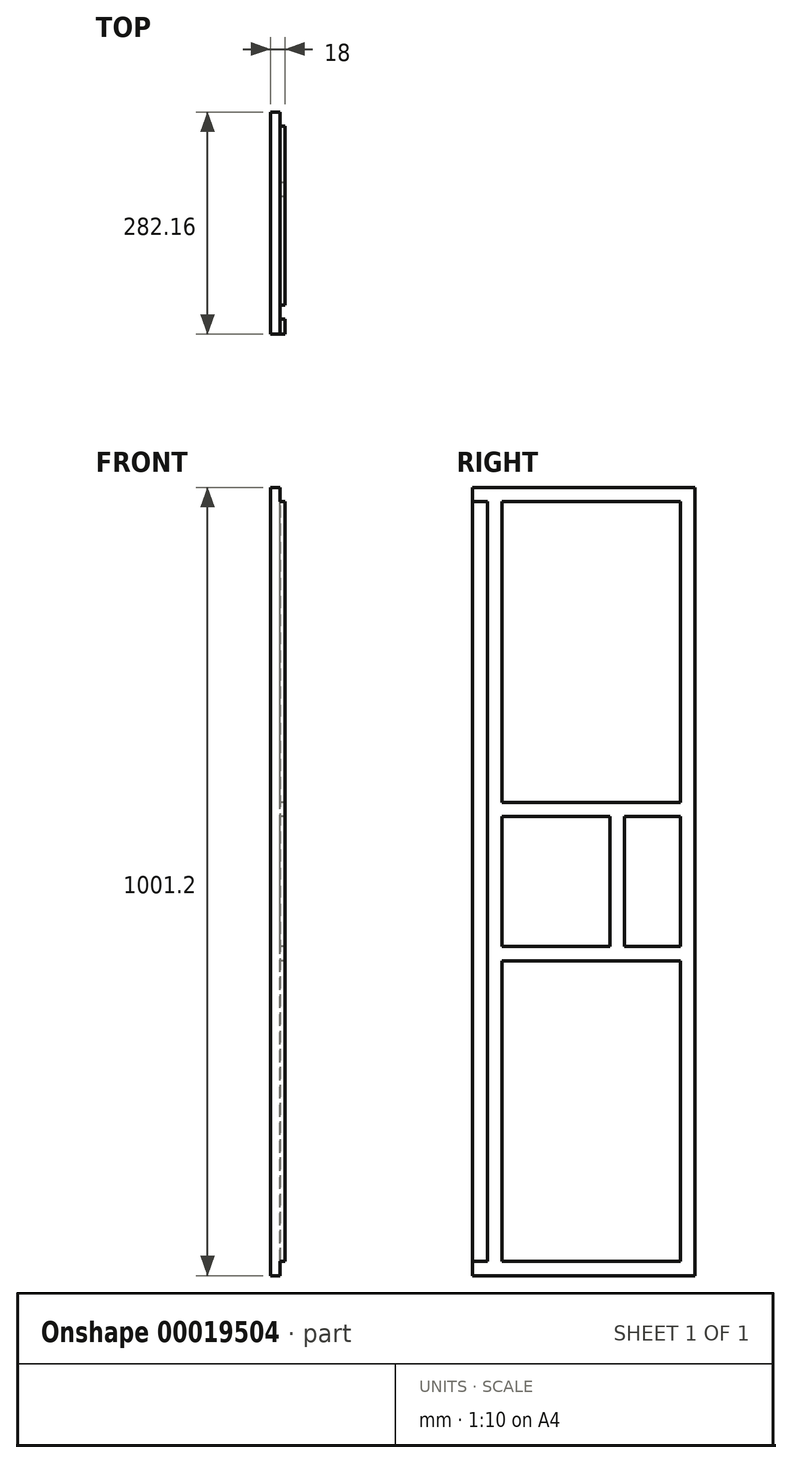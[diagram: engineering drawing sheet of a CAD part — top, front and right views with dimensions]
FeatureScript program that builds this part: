
annotation { "Feature Type Name" : "Feature", "Feature Type Description" : "" }
export const myFeature = defineFeature(function(context is Context, id is Id, definition is map)
    precondition{}
    {
        {
            var Q0;
            Q0=qCreatedBy(makeId("Right.planeOp"),FACE);
            var sketch = newSketch(context, id + "F0", { "sketchPlane" : qUnion([Q0])});
            skLineSegment(sketch, "E0.bottom", {"start": v(-347.26, 666.81) * mm, "end": v(-65.1, 666.81) * mm});
            skLineSegment(sketch, "E0.top", {"start": v(-347.26, -334.39) * mm, "end": v(-65.1, -334.39) * mm});
            skLineSegment(sketch, "E0.left", {"start": v(-347.26, 666.81) * mm, "end": v(-347.26, -334.39) * mm});
            skLineSegment(sketch, "E0.right", {"start": v(-65.1, 666.81) * mm, "end": v(-65.1, -334.39) * mm});
            skSolve(sketch);
        }
        {
            var Q0;
            Q0 = qSketchRegion(id + "F0", true);
            extrude(context, id + "F1", {"entities" : qUnion([Q0]), "depth" : 18 * mm});
        }
        {
            var Q0;
            Q0=makeQuery(id+"F1.opExtrude","CAP_FACE",FACE,{"disambiguationData":[OSD([sQuery(id+"F0.wireOp",EDGE,"E0.bottom"),sQuery(id+"F0.wireOp",EDGE,"E0.top"),sQuery(id+"F0.wireOp",EDGE,"E0.left"),sQuery(id+"F0.wireOp",EDGE,"E0.right")])],"isStart":false});
            var sketch = newSketch(context, id + "F2", { "sketchPlane" : qUnion([Q0])});
            skLineSegment(sketch, "E1.bottom", {"start": v(-328.2, -334.39) * mm, "end": v(-310.2, -334.39) * mm});
            skLineSegment(sketch, "E1.top", {"start": v(-328.2, 666.81) * mm, "end": v(-310.2, 666.81) * mm});
            skLineSegment(sketch, "E1.left", {"start": v(-328.2, -334.39) * mm, "end": v(-328.2, 666.81) * mm});
            skLineSegment(sketch, "E1.right", {"start": v(-310.2, -334.39) * mm, "end": v(-310.2, 666.81) * mm});
            skSolve(sketch);
        }
        {
            var Q0;
            Q0 = qSketchRegion(id + "F2", true);
            extrude(context, id + "F3", {"entities" : qUnion([Q0]), "operationType" : NewBodyOperationType.REMOVE, "oppositeDirection" : true, "depth" : 6 * mm});
        }
        {
            var Q0;
            {var subQ0=sQuery(id+"F0.wireOp",EDGE,"E0.bottom");var subQ1=sQuery(id+"F0.wireOp",EDGE,"E0.top");var subQ2=sQuery(id+"F0.wireOp",EDGE,"E0.right");Q0=makeQuery(id+"F3.boolean.opBoolean","SPLIT",FACE,{"disambiguationData":[TD([makeQuery(id+"F1.opExtrude","SWEPT_FACE",FACE,{"disambiguationData":[OSD([subQ2])]})])],"derivedFrom":makeQuery(id+"F1.opExtrude","CAP_FACE",FACE,{"disambiguationData":[OSD([subQ0,subQ1,sQuery(id+"F0.wireOp",EDGE,"E0.left"),subQ2])],"isStart":false})});}
            var sketch = newSketch(context, id + "F4", { "sketchPlane" : qUnion([Q0])});
            skLineSegment(sketch, "E2.bottom", {"start": v(-65.1, 666.81) * mm, "end": v(-83.1, 666.81) * mm});
            skLineSegment(sketch, "E2.top", {"start": v(-65.1, -334.39) * mm, "end": v(-83.1, -334.39) * mm});
            skLineSegment(sketch, "E2.left", {"start": v(-65.1, 666.81) * mm, "end": v(-65.1, -334.39) * mm});
            skLineSegment(sketch, "E2.right", {"start": v(-83.1, 666.81) * mm, "end": v(-83.1, -334.39) * mm});
            skSolve(sketch);
        }
        {
            var Q0;
            Q0 = qSketchRegion(id + "F4", true);
            extrude(context, id + "F5", {"entities" : qUnion([Q0]), "operationType" : NewBodyOperationType.REMOVE, "oppositeDirection" : true, "depth" : 6 * mm});
        }
        {
            var Q0;
            Q0=makeQuery(id+"F5.boolean.opBoolean","COPY",FACE,{"derivedFrom":makeQuery(id+"F5.opExtrude","CAP_FACE",FACE,{"disambiguationData":[OSD([sQuery(id+"F4.wireOp",EDGE,"E2.bottom"),sQuery(id+"F4.wireOp",EDGE,"E2.top"),sQuery(id+"F4.wireOp",EDGE,"E2.left"),sQuery(id+"F4.wireOp",EDGE,"E2.right")])],"isStart":false})});
            var sketch = newSketch(context, id + "F6", { "sketchPlane" : qUnion([Q0])});
            skLineSegment(sketch, "E3.bottom", {"start": v(-65.1, 666.81) * mm, "end": v(-573.1, 666.81) * mm});
            skLineSegment(sketch, "E3.top", {"start": v(-65.1, 648.81) * mm, "end": v(-573.1, 648.81) * mm});
            skLineSegment(sketch, "E3.left", {"start": v(-65.1, 666.81) * mm, "end": v(-65.1, 648.81) * mm});
            skLineSegment(sketch, "E3.right", {"start": v(-573.1, 666.81) * mm, "end": v(-573.1, 648.81) * mm});
            skLineSegment(sketch, "E4.bottom", {"start": v(-65.1, -334.39) * mm, "end": v(-532.01, -334.39) * mm});
            skLineSegment(sketch, "E4.top", {"start": v(-65.1, -316.39) * mm, "end": v(-532.01, -316.39) * mm});
            skLineSegment(sketch, "E4.left", {"start": v(-65.1, -334.39) * mm, "end": v(-65.1, -316.39) * mm});
            skLineSegment(sketch, "E4.right", {"start": v(-532.01, -334.39) * mm, "end": v(-532.01, -316.39) * mm});
            skSolve(sketch);
        }
        {
            var Q0;
            Q0 = qSketchRegion(id + "F6", true);
            extrude(context, id + "F7", {"entities" : qUnion([Q0]), "operationType" : NewBodyOperationType.REMOVE, "depth" : 6 * mm});
        }
        {
            var Q0;
            {var subQ0=sQuery(id+"F0.wireOp",EDGE,"E0.bottom");var subQ1=sQuery(id+"F0.wireOp",EDGE,"E0.top");var subQ2=sQuery(id+"F0.wireOp",EDGE,"E0.right");Q0=makeQuery(id+"F3.boolean.opBoolean","SPLIT",FACE,{"disambiguationData":[TD([makeQuery(id+"F1.opExtrude","SWEPT_FACE",FACE,{"disambiguationData":[OSD([subQ2])]})])],"derivedFrom":makeQuery(id+"F1.opExtrude","CAP_FACE",FACE,{"disambiguationData":[OSD([subQ0,subQ1,sQuery(id+"F0.wireOp",EDGE,"E0.left"),subQ2])],"isStart":false})});}
            var sketch = newSketch(context, id + "F8", { "sketchPlane" : qUnion([Q0])});
            skLineSegment(sketch, "E5", {"start": v(-310.2, 166.21) * mm, "end": v(-83.1, 166.21) * mm, "construction": true});
            skLineSegment(sketch, "E6.bottom", {"start": v(-328.2, 266.76) * mm, "end": v(193.38, 266.76) * mm});
            skLineSegment(sketch, "E6.top", {"start": v(-328.2, 248.76) * mm, "end": v(193.38, 248.76) * mm});
            skLineSegment(sketch, "E6.left", {"start": v(-328.2, 266.76) * mm, "end": v(-328.2, 248.76) * mm});
            skLineSegment(sketch, "E6.right", {"start": v(193.38, 266.76) * mm, "end": v(193.38, 248.76) * mm});
            skLineSegment(sketch, "E7.bottom", {"start": v(-328.2, 83.66) * mm, "end": v(173.7, 83.66) * mm});
            skLineSegment(sketch, "E7.top", {"start": v(-328.2, 65.66) * mm, "end": v(173.7, 65.66) * mm});
            skLineSegment(sketch, "E7.left", {"start": v(-328.2, 83.66) * mm, "end": v(-328.2, 65.66) * mm});
            skLineSegment(sketch, "E7.right", {"start": v(173.7, 83.66) * mm, "end": v(173.7, 65.66) * mm});
            skSolve(sketch);
        }
        {
            var Q0;
            Q0 = qSketchRegion(id + "F8", true);
            extrude(context, id + "F9", {"entities" : qUnion([Q0]), "operationType" : NewBodyOperationType.REMOVE, "oppositeDirection" : true, "depth" : 6 * mm});
        }
        {
            var Q0;
            {var subQ0=sQuery(id+"F0.wireOp",EDGE,"E0.bottom");var subQ1=sQuery(id+"F0.wireOp",EDGE,"E0.top");var subQ2=sQuery(id+"F0.wireOp",EDGE,"E0.right");Q0=makeQuery(id+"F9.boolean.opBoolean","SPLIT",FACE,{"disambiguationData":[TD([makeQuery(id+"F9.opExtrude","SWEPT_FACE",FACE,{"disambiguationData":[OSD([sQuery(id+"F8.wireOp",EDGE,"E6.top")])]})])],"derivedFrom":makeQuery(id+"F3.boolean.opBoolean","SPLIT",FACE,{"disambiguationData":[TD([makeQuery(id+"F1.opExtrude","SWEPT_FACE",FACE,{"disambiguationData":[OSD([subQ2])]})])],"derivedFrom":makeQuery(id+"F1.opExtrude","CAP_FACE",FACE,{"disambiguationData":[OSD([subQ0,subQ1,sQuery(id+"F0.wireOp",EDGE,"E0.left"),subQ2])],"isStart":false})})});}
            var sketch = newSketch(context, id + "F10", { "sketchPlane" : qUnion([Q0])});
            skLineSegment(sketch, "E8.bottom", {"start": v(-172.63, 252.99) * mm, "end": v(-154.63, 252.99) * mm});
            skLineSegment(sketch, "E8.top", {"start": v(-172.63, 75.19) * mm, "end": v(-154.63, 75.19) * mm});
            skLineSegment(sketch, "E8.left", {"start": v(-172.63, 252.99) * mm, "end": v(-172.63, 75.19) * mm});
            skLineSegment(sketch, "E8.right", {"start": v(-154.63, 252.99) * mm, "end": v(-154.63, 75.19) * mm});
            skSolve(sketch);
        }
        {
            var Q0;
            Q0 = qSketchRegion(id + "F10", true);
            extrude(context, id + "F11", {"entities" : qUnion([Q0]), "operationType" : NewBodyOperationType.REMOVE, "oppositeDirection" : true, "depth" : 6 * mm});
        }
    });
